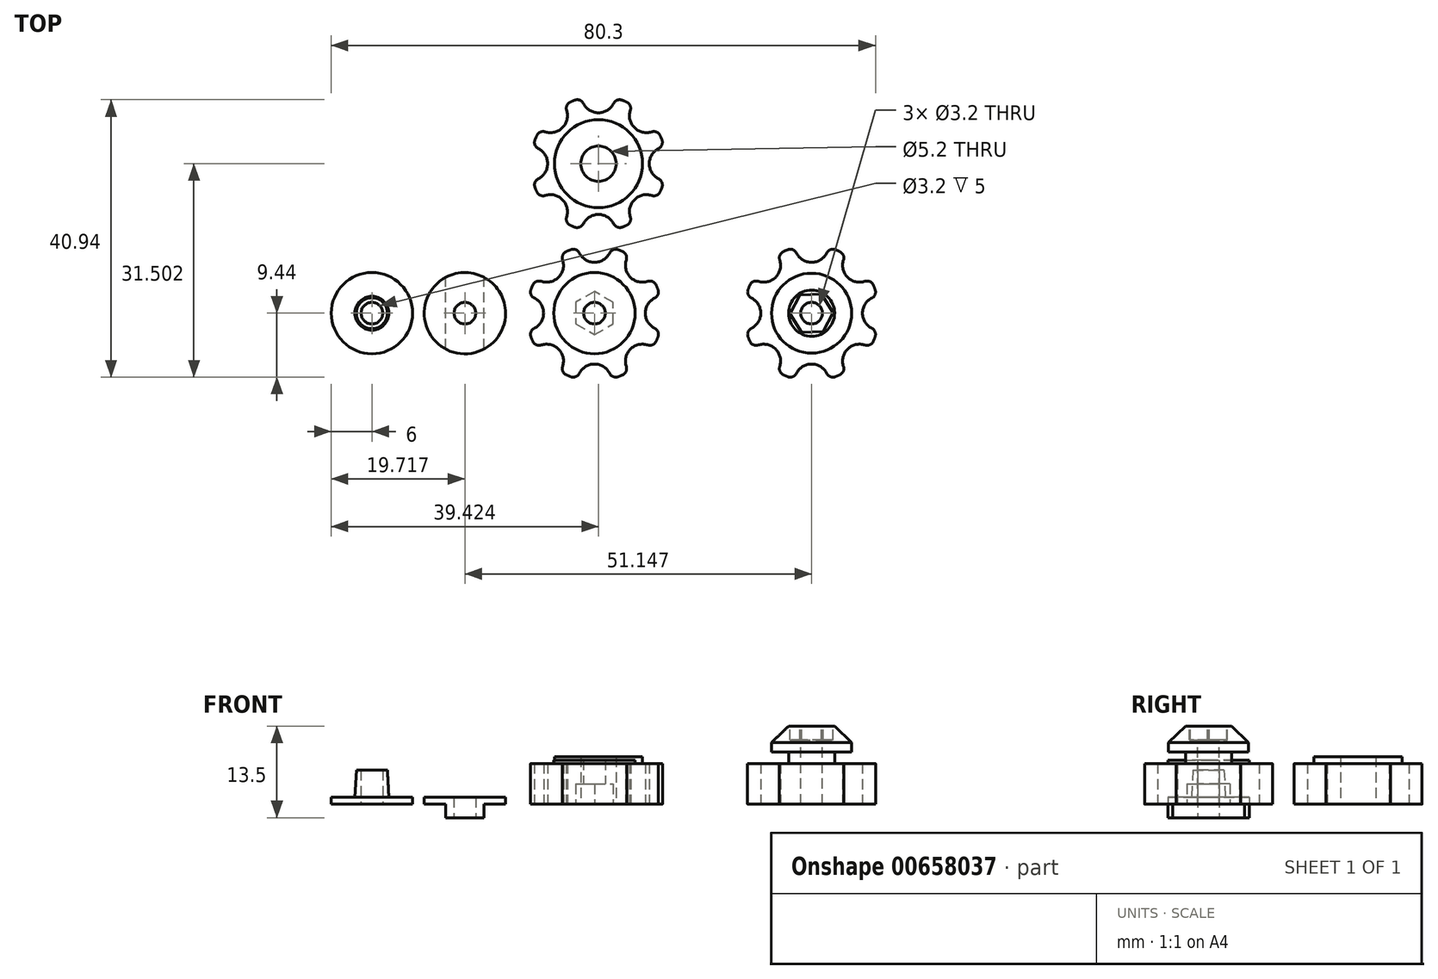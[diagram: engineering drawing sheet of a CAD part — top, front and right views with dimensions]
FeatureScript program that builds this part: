
annotation { "Feature Type Name" : "Feature", "Feature Type Description" : "" }
export const myFeature = defineFeature(function(context is Context, id is Id, definition is map)
    precondition{}
    {
        {
            var Q0;
            Q0=qCreatedBy(makeId("Top.planeOp"),FACE);
            var sketch = newSketch(context, id + "F0", { "sketchPlane" : qUnion([Q0])});
            skCircle(sketch, "E0", {"center": v(0, 0) * mm, "radius": 6 * mm});
            skSolve(sketch);
        }
        {
            var Q0;
            Q0 = qSketchRegion(id + "F0", true);
            extrude(context, id + "F1", {"entities" : qUnion([Q0]), "depth" : 1 * mm, "offsetDistance" : 25 * mm});
        }
        {
            var Q0;
            Q0=makeQuery(id+"F1.opExtrude","CAP_FACE",FACE,{"disambiguationData":[OSD([sQuery(id+"F0.wireOp",EDGE,"E0")])],"isStart":false});
            var sketch = newSketch(context, id + "F2", { "sketchPlane" : qUnion([Q0])});
            skCircle(sketch, "E1", {"center": v(0, 0) * mm, "radius": 2.5 * mm});
            skSolve(sketch);
        }
        {
            var Q0;
            Q0 = qSketchRegion(id + "F2", true);
            extrude(context, id + "F3", {"entities" : qUnion([Q0]), "operationType" : NewBodyOperationType.ADD, "depth" : 4 * mm, "offsetDistance" : 25 * mm, "hasDraft" : true, "draftAngle" : 3 * degree, "draftPullDirection" : true});
        }
        {
            var Q0;
            Q0=makeQuery(id+"F1.opExtrude","CAP_FACE",FACE,{"disambiguationData":[OSD([sQuery(id+"F0.wireOp",EDGE,"E0")])],"isStart":true});
            var sketch = newSketch(context, id + "F4", { "sketchPlane" : qUnion([Q0])});
            skCircle(sketch, "E2", {"center": v(0, 0) * mm, "radius": 1.6 * mm});
            skSolve(sketch);
        }
        {
            var Q0;
            Q0 = qSketchRegion(id + "F4", true);
            extrude(context, id + "F5", {"entities" : qUnion([Q0]), "operationType" : NewBodyOperationType.REMOVE, "oppositeDirection" : true, "depth" : 25 * mm, "offsetDistance" : 25 * mm});
        }
        {
            var Q0;
            Q0=qCreatedBy(makeId("Top.planeOp"),FACE);
            var sketch = newSketch(context, id + "F6", { "sketchPlane" : qUnion([Q0])});
            skCircle(sketch, "E3", {"center": v(13.72, 0) * mm, "radius": 6 * mm});
            skCircle(sketch, "E4", {"center": v(13.72, 0) * mm, "radius": 1.6 * mm});
            skSolve(sketch);
        }
        {
            var Q0;
            Q0 = qSketchRegion(id + "F6", true);
            extrude(context, id + "F7", {"entities" : qUnion([Q0]), "depth" : 1 * mm, "offsetDistance" : 25 * mm});
        }
        {
            var Q0;
            Q0=makeQuery(id+"F7.opExtrude","CAP_FACE",FACE,{"disambiguationData":[OSD([sQuery(id+"F6.wireOp",EDGE,"E3"),sQuery(id+"F6.wireOp",EDGE,"E4")])],"isStart":true});
            var sketch = newSketch(context, id + "F8", { "sketchPlane" : qUnion([Q0])});
            skLineSegment(sketch, "E5", {"start": v(13.72, 0) * mm, "end": v(13.72, 6) * mm, "construction": true});
            skLineSegment(sketch, "E6", {"start": v(10.92, 5.3) * mm, "end": v(10.92, -5.3) * mm});
            skLineSegment(sketch, "E7.MirrorCS", {"start": v(16.52, 5.3) * mm, "end": v(16.52, -5.3) * mm});
            skArc(sketch, "E8", {"start": v(16.52, 5.3) * mm, "mid": v(13.72, 6) * mm, "end": v(10.92, 5.3) * mm, "construction": true});
            skArc(sketch, "E9.trimOffspring", {"start": v(10.92, -5.3) * mm, "mid": v(13.72, -6) * mm, "end": v(16.52, -5.3) * mm, "construction": true});
            skCircle(sketch, "E10", {"center": v(13.72, 0) * mm, "radius": 1.6 * mm});
            skSolve(sketch);
        }
        {
            var Q0;
            {var subQ0=sQuery(id+"F8.wireOp",EDGE,"E6");Q0=makeQuery(id+"F8.imprint","IMPRINT",FACE,{"disambiguationData":[TD([[makeQuery(id+"F8.imprint","IMPRINT",EDGE,{"derivedFrom":subQ0}),1.0]])]});}
            extrude(context, id + "F9", {"entities" : qUnion([Q0]), "operationType" : NewBodyOperationType.ADD, "depth" : 2 * mm, "offsetDistance" : 25 * mm});
        }
        {
            var Q0;
            Q0=qCreatedBy(makeId("Top.planeOp"),FACE);
            var sketch = newSketch(context, id + "F10", { "sketchPlane" : qUnion([Q0])});
            skArc(sketch, "E11", {"start": v(37, 9.09) * mm, "mid": v(36.66, 9.24) * mm, "end": v(36.31, 9.38) * mm});
            skCircle(sketch, "E12", {"center": v(32.83, 0) * mm, "radius": 1.6 * mm});
            skArc(sketch, "E13", {"start": v(41.72, 2.24) * mm, "mid": v(40.33, 0) * mm, "end": v(41.72, -2.24) * mm});
            skArc(sketch, "E14.1.0", {"start": v(37.53, 7.86) * mm, "mid": v(38.14, 5.3) * mm, "end": v(40.7, 4.7) * mm});
            skArc(sketch, "E14.2.0", {"start": v(30.6, 8.88) * mm, "mid": v(32.83, 7.5) * mm, "end": v(35.07, 8.88) * mm});
            skArc(sketch, "E14.3.0", {"start": v(24.97, 4.7) * mm, "mid": v(27.53, 5.3) * mm, "end": v(28.13, 7.86) * mm});
            skArc(sketch, "E14.4.0", {"start": v(23.95, -2.24) * mm, "mid": v(25.33, 0) * mm, "end": v(23.95, 2.24) * mm});
            skArc(sketch, "E14.5.0", {"start": v(28.13, -7.86) * mm, "mid": v(27.53, -5.3) * mm, "end": v(24.97, -4.7) * mm});
            skArc(sketch, "E14.6.0", {"start": v(35.07, -8.88) * mm, "mid": v(32.83, -7.5) * mm, "end": v(30.6, -8.88) * mm});
            skArc(sketch, "E14.7.0", {"start": v(40.7, -4.7) * mm, "mid": v(38.14, -5.3) * mm, "end": v(37.53, -7.86) * mm});
            skArc(sketch, "E15.trimOffspring", {"start": v(42.2, 3.48) * mm, "mid": v(42.07, 3.83) * mm, "end": v(41.92, 4.17) * mm});
            skArc(sketch, "E16.trimOffspring", {"start": v(41.92, -4.17) * mm, "mid": v(42.07, -3.83) * mm, "end": v(42.2, -3.48) * mm});
            skArc(sketch, "E17.trimOffspring", {"start": v(36.31, -9.38) * mm, "mid": v(36.66, -9.24) * mm, "end": v(37, -9.09) * mm});
            skArc(sketch, "E18.trimOffspring", {"start": v(28.66, -9.09) * mm, "mid": v(29, -9.24) * mm, "end": v(29.35, -9.38) * mm});
            skArc(sketch, "E19.trimOffspring", {"start": v(23.46, -3.48) * mm, "mid": v(23.6, -3.83) * mm, "end": v(23.74, -4.17) * mm});
            skArc(sketch, "E20.trimOffspring", {"start": v(23.74, 4.17) * mm, "mid": v(23.6, 3.83) * mm, "end": v(23.46, 3.48) * mm});
            skArc(sketch, "E21.trimOffspring", {"start": v(29.35, 9.38) * mm, "mid": v(29, 9.24) * mm, "end": v(28.66, 9.09) * mm});
            skPoint(sketch, "E22.visualSharp", {"position": v(37.93, 8.6) * mm});
            skArc(sketch, "E22.filletArc", {"start": v(37.53, 7.86) * mm, "mid": v(37.5, 8.58) * mm, "end": v(37, 9.09) * mm});
            skPoint(sketch, "E23.visualSharp", {"position": v(35.31, 9.69) * mm});
            skArc(sketch, "E23.filletArc", {"start": v(36.31, 9.38) * mm, "mid": v(35.6, 9.37) * mm, "end": v(35.07, 8.88) * mm});
            skPoint(sketch, "E24.visualSharp", {"position": v(30.35, 9.69) * mm});
            skArc(sketch, "E24.filletArc", {"start": v(30.6, 8.88) * mm, "mid": v(30.07, 9.37) * mm, "end": v(29.35, 9.38) * mm});
            skPoint(sketch, "E25.visualSharp", {"position": v(27.74, 8.6) * mm});
            skArc(sketch, "E25.filletArc", {"start": v(28.66, 9.09) * mm, "mid": v(28.16, 8.58) * mm, "end": v(28.13, 7.86) * mm});
            skPoint(sketch, "E26.visualSharp", {"position": v(24.23, 5.1) * mm});
            skArc(sketch, "E26.filletArc", {"start": v(24.97, 4.7) * mm, "mid": v(24.25, 4.67) * mm, "end": v(23.74, 4.17) * mm});
            skPoint(sketch, "E27.visualSharp", {"position": v(23.15, 2.48) * mm});
            skArc(sketch, "E27.filletArc", {"start": v(23.46, 3.48) * mm, "mid": v(23.47, 2.76) * mm, "end": v(23.95, 2.24) * mm});
            skPoint(sketch, "E28.visualSharp", {"position": v(23.15, -2.48) * mm});
            skArc(sketch, "E28.filletArc", {"start": v(23.95, -2.24) * mm, "mid": v(23.47, -2.76) * mm, "end": v(23.46, -3.48) * mm});
            skPoint(sketch, "E29.visualSharp", {"position": v(24.23, -5.1) * mm});
            skArc(sketch, "E29.filletArc", {"start": v(23.74, -4.17) * mm, "mid": v(24.25, -4.67) * mm, "end": v(24.97, -4.7) * mm});
            skPoint(sketch, "E30.visualSharp", {"position": v(27.74, -8.6) * mm});
            skArc(sketch, "E30.filletArc", {"start": v(28.13, -7.86) * mm, "mid": v(28.16, -8.58) * mm, "end": v(28.66, -9.09) * mm});
            skPoint(sketch, "E31.visualSharp", {"position": v(30.35, -9.69) * mm});
            skArc(sketch, "E31.filletArc", {"start": v(29.35, -9.38) * mm, "mid": v(30.07, -9.37) * mm, "end": v(30.6, -8.88) * mm});
            skPoint(sketch, "E32.visualSharp", {"position": v(35.31, -9.69) * mm});
            skArc(sketch, "E32.filletArc", {"start": v(35.07, -8.88) * mm, "mid": v(35.6, -9.37) * mm, "end": v(36.31, -9.38) * mm});
            skPoint(sketch, "E33.visualSharp", {"position": v(37.93, -8.6) * mm});
            skArc(sketch, "E33.filletArc", {"start": v(37, -9.09) * mm, "mid": v(37.5, -8.58) * mm, "end": v(37.53, -7.86) * mm});
            skPoint(sketch, "E34.visualSharp", {"position": v(41.44, -5.1) * mm});
            skArc(sketch, "E34.filletArc", {"start": v(40.7, -4.7) * mm, "mid": v(41.41, -4.67) * mm, "end": v(41.92, -4.17) * mm});
            skPoint(sketch, "E35.visualSharp", {"position": v(42.52, -2.48) * mm});
            skArc(sketch, "E35.filletArc", {"start": v(42.2, -3.48) * mm, "mid": v(42.2, -2.76) * mm, "end": v(41.72, -2.24) * mm});
            skPoint(sketch, "E36.visualSharp", {"position": v(42.52, 2.48) * mm});
            skArc(sketch, "E36.filletArc", {"start": v(41.72, 2.24) * mm, "mid": v(42.2, 2.76) * mm, "end": v(42.2, 3.48) * mm});
            skPoint(sketch, "E37.visualSharp", {"position": v(41.44, 5.1) * mm});
            skArc(sketch, "E37.filletArc", {"start": v(41.92, 4.17) * mm, "mid": v(41.41, 4.67) * mm, "end": v(40.7, 4.7) * mm});
            skSolve(sketch);
        }
        {
            var Q0;
            Q0 = qSketchRegion(id + "F10", true);
            extrude(context, id + "F11", {"entities" : qUnion([Q0]), "depth" : 6 * mm, "offsetDistance" : 25 * mm});
        }
        {
            var Q0;
            Q0=makeQuery(id+"F11.opExtrude","CAP_FACE",FACE,{"disambiguationData":[OSD([sQuery(id+"F10.wireOp",EDGE,"E11"),sQuery(id+"F10.wireOp",EDGE,"E12"),sQuery(id+"F10.wireOp",EDGE,"E13"),sQuery(id+"F10.wireOp",EDGE,"E14.1.0"),sQuery(id+"F10.wireOp",EDGE,"E14.2.0"),sQuery(id+"F10.wireOp",EDGE,"E14.3.0"),sQuery(id+"F10.wireOp",EDGE,"E14.4.0"),sQuery(id+"F10.wireOp",EDGE,"E14.5.0"),sQuery(id+"F10.wireOp",EDGE,"E14.6.0"),sQuery(id+"F10.wireOp",EDGE,"E14.7.0"),sQuery(id+"F10.wireOp",EDGE,"E15.trimOffspring"),sQuery(id+"F10.wireOp",EDGE,"E16.trimOffspring"),sQuery(id+"F10.wireOp",EDGE,"E17.trimOffspring"),sQuery(id+"F10.wireOp",EDGE,"E18.trimOffspring"),sQuery(id+"F10.wireOp",EDGE,"E19.trimOffspring"),sQuery(id+"F10.wireOp",EDGE,"E20.trimOffspring"),sQuery(id+"F10.wireOp",EDGE,"E21.trimOffspring"),sQuery(id+"F10.wireOp",EDGE,"E22.filletArc"),sQuery(id+"F10.wireOp",EDGE,"E23.filletArc"),sQuery(id+"F10.wireOp",EDGE,"E24.filletArc"),sQuery(id+"F10.wireOp",EDGE,"E25.filletArc"),sQuery(id+"F10.wireOp",EDGE,"E26.filletArc"),sQuery(id+"F10.wireOp",EDGE,"E27.filletArc"),sQuery(id+"F10.wireOp",EDGE,"E28.filletArc"),sQuery(id+"F10.wireOp",EDGE,"E29.filletArc"),sQuery(id+"F10.wireOp",EDGE,"E30.filletArc"),sQuery(id+"F10.wireOp",EDGE,"E31.filletArc"),sQuery(id+"F10.wireOp",EDGE,"E32.filletArc"),sQuery(id+"F10.wireOp",EDGE,"E33.filletArc"),sQuery(id+"F10.wireOp",EDGE,"E34.filletArc"),sQuery(id+"F10.wireOp",EDGE,"E35.filletArc"),sQuery(id+"F10.wireOp",EDGE,"E36.filletArc"),sQuery(id+"F10.wireOp",EDGE,"E37.filletArc")])],"isStart":false});
            var sketch = newSketch(context, id + "F12", { "sketchPlane" : qUnion([Q0])});
            skCircle(sketch, "E38", {"center": v(32.83, 0) * mm, "radius": 1.6 * mm});
            skCircle(sketch, "E39", {"center": v(32.83, 0) * mm, "radius": 6 * mm});
            skSolve(sketch);
        }
        {
            var Q0;
            Q0=makeQuery(id+"F12.imprint","IMPRINT",FACE,{"disambiguationData":[TD([[makeQuery(id+"F12.imprint","IMPRINT",EDGE,{"derivedFrom":sQuery(id+"F12.wireOp",EDGE,"E38")}),-1.0]])]});
            extrude(context, id + "F13", {"entities" : qUnion([Q0]), "operationType" : NewBodyOperationType.ADD, "depth" : 0.5 * mm, "offsetDistance" : 25 * mm});
        }
        {
            var Q0;
            Q0=makeQuery(id+"F11.opExtrude","CAP_FACE",FACE,{"disambiguationData":[OSD([sQuery(id+"F10.wireOp",EDGE,"E11"),sQuery(id+"F10.wireOp",EDGE,"E12"),sQuery(id+"F10.wireOp",EDGE,"E13"),sQuery(id+"F10.wireOp",EDGE,"E14.1.0"),sQuery(id+"F10.wireOp",EDGE,"E14.2.0"),sQuery(id+"F10.wireOp",EDGE,"E14.3.0"),sQuery(id+"F10.wireOp",EDGE,"E14.4.0"),sQuery(id+"F10.wireOp",EDGE,"E14.5.0"),sQuery(id+"F10.wireOp",EDGE,"E14.6.0"),sQuery(id+"F10.wireOp",EDGE,"E14.7.0"),sQuery(id+"F10.wireOp",EDGE,"E15.trimOffspring"),sQuery(id+"F10.wireOp",EDGE,"E16.trimOffspring"),sQuery(id+"F10.wireOp",EDGE,"E17.trimOffspring"),sQuery(id+"F10.wireOp",EDGE,"E18.trimOffspring"),sQuery(id+"F10.wireOp",EDGE,"E19.trimOffspring"),sQuery(id+"F10.wireOp",EDGE,"E20.trimOffspring"),sQuery(id+"F10.wireOp",EDGE,"E21.trimOffspring"),sQuery(id+"F10.wireOp",EDGE,"E22.filletArc"),sQuery(id+"F10.wireOp",EDGE,"E23.filletArc"),sQuery(id+"F10.wireOp",EDGE,"E24.filletArc"),sQuery(id+"F10.wireOp",EDGE,"E25.filletArc"),sQuery(id+"F10.wireOp",EDGE,"E26.filletArc"),sQuery(id+"F10.wireOp",EDGE,"E27.filletArc"),sQuery(id+"F10.wireOp",EDGE,"E28.filletArc"),sQuery(id+"F10.wireOp",EDGE,"E29.filletArc"),sQuery(id+"F10.wireOp",EDGE,"E30.filletArc"),sQuery(id+"F10.wireOp",EDGE,"E31.filletArc"),sQuery(id+"F10.wireOp",EDGE,"E32.filletArc"),sQuery(id+"F10.wireOp",EDGE,"E33.filletArc"),sQuery(id+"F10.wireOp",EDGE,"E34.filletArc"),sQuery(id+"F10.wireOp",EDGE,"E35.filletArc"),sQuery(id+"F10.wireOp",EDGE,"E36.filletArc"),sQuery(id+"F10.wireOp",EDGE,"E37.filletArc")])],"isStart":true});
            var sketch = newSketch(context, id + "F14", { "sketchPlane" : qUnion([Q0])});
            skCircle(sketch, "E40.cCircle", {"center": v(32.83, 0) * mm, "radius": 2.75 * mm, "construction": true});
            skLineSegment(sketch, "E40.0", {"start": v(35.58, 1.59) * mm, "end": v(35.58, -1.59) * mm});
            skLineSegment(sketch, "E40.1", {"start": v(35.58, -1.59) * mm, "end": v(32.83, -3.18) * mm});
            skLineSegment(sketch, "E40.2", {"start": v(32.83, -3.18) * mm, "end": v(30.08, -1.59) * mm});
            skLineSegment(sketch, "E40.3", {"start": v(30.08, -1.59) * mm, "end": v(30.08, 1.59) * mm});
            skLineSegment(sketch, "E40.4", {"start": v(30.08, 1.59) * mm, "end": v(32.83, 3.18) * mm});
            skLineSegment(sketch, "E40.5", {"start": v(32.83, 3.18) * mm, "end": v(35.58, 1.59) * mm});
            skPoint(sketch, "E40.0.midPoint", {"position": v(35.58, 0) * mm});
            skSolve(sketch);
        }
        {
            var Q0;
            Q0 = qSketchRegion(id + "F14", true);
            extrude(context, id + "F15", {"entities" : qUnion([Q0]), "operationType" : NewBodyOperationType.REMOVE, "oppositeDirection" : true, "depth" : 3 * mm, "offsetDistance" : 25 * mm});
        }
        {
            var Q0;
            Q0=qCreatedBy(makeId("Front.planeOp"),FACE);
            var sketch = newSketch(context, id + "F16", { "sketchPlane" : qUnion([Q0])});
            skLineSegment(sketch, "E41", {"start": v(64.86, 11.5) * mm, "end": v(68.26, 11.5) * mm});
            skLineSegment(sketch, "E42", {"start": v(68.26, 11.5) * mm, "end": v(70.76, 9.1) * mm});
            skLineSegment(sketch, "E43", {"start": v(70.76, 9.1) * mm, "end": v(70.76, 7.7) * mm});
            skLineSegment(sketch, "E44", {"start": v(70.76, 7.7) * mm, "end": v(68.26, 7.7) * mm});
            skLineSegment(sketch, "E45", {"start": v(68.26, 7.7) * mm, "end": v(68.26, 6) * mm});
            skLineSegment(sketch, "E46", {"start": v(68.26, 6) * mm, "end": v(74.86, 6) * mm});
            skLineSegment(sketch, "E47", {"start": v(74.86, 6) * mm, "end": v(74.86, 0) * mm});
            skLineSegment(sketch, "E48", {"start": v(74.86, 0) * mm, "end": v(64.86, 0) * mm});
            skLineSegment(sketch, "E49", {"start": v(64.86, 0) * mm, "end": v(64.86, 11.5) * mm});
            skSolve(sketch);
        }
        {
            var Q0;
            Q0 = qSketchRegion(id + "F16", true);
            var Q1;
            Q1=sQuery(id+"F16.wireOp",EDGE,"E49");
            revolve(context, id + "F17", {"operationType" : NewBodyOperationType.ADD, "surfaceOperationType" : NewSurfaceOperationType.NEW, "entities" : qUnion([Q0]), "axis" : qUnion([Q1]), "revolveType" : RevolveType.FULL});
        }
        {
            var Q0;
            Q0=makeQuery(id+"F17.opRevolve","SWEPT_FACE",FACE,{"disambiguationData":[OSD([sQuery(id+"F16.wireOp",EDGE,"E41")])]});
            var sketch = newSketch(context, id + "F18", { "sketchPlane" : qUnion([Q0])});
            skCircle(sketch, "E50", {"center": v(64.86, 0) * mm, "radius": 1.6 * mm});
            skSolve(sketch);
        }
        {
            var Q0;
            Q0 = qSketchRegion(id + "F18", true);
            extrude(context, id + "F19", {"entities" : qUnion([Q0]), "operationType" : NewBodyOperationType.REMOVE, "oppositeDirection" : true, "depth" : 25 * mm, "offsetDistance" : 25 * mm});
        }
        {
            var Q0;
            Q0=makeQuery(id+"F17.opRevolve","SWEPT_FACE",FACE,{"disambiguationData":[OSD([sQuery(id+"F16.wireOp",EDGE,"E41")])]});
            var sketch = newSketch(context, id + "F20", { "sketchPlane" : qUnion([Q0])});
            skCircle(sketch, "E51.cCircle", {"center": v(64.86, 0) * mm, "radius": 2.75 * mm, "construction": true});
            skLineSegment(sketch, "E51.0", {"start": v(68.04, 0.12) * mm, "end": v(66.56, -2.69) * mm});
            skLineSegment(sketch, "E51.1", {"start": v(66.56, -2.69) * mm, "end": v(63.38, -2.8) * mm});
            skLineSegment(sketch, "E51.2", {"start": v(63.38, -2.8) * mm, "end": v(61.7, -0.12) * mm});
            skLineSegment(sketch, "E51.3", {"start": v(61.7, -0.12) * mm, "end": v(63.17, 2.69) * mm});
            skLineSegment(sketch, "E51.4", {"start": v(63.17, 2.69) * mm, "end": v(66.34, 2.8) * mm});
            skLineSegment(sketch, "E51.5", {"start": v(66.34, 2.8) * mm, "end": v(68.04, 0.12) * mm});
            skPoint(sketch, "E51.0.midPoint", {"position": v(67.3, -1.28) * mm});
            skSolve(sketch);
        }
        {
            var Q0;
            Q0 = qSketchRegion(id + "F20", true);
            extrude(context, id + "F21", {"entities" : qUnion([Q0]), "operationType" : NewBodyOperationType.REMOVE, "oppositeDirection" : true, "depth" : 2 * mm, "offsetDistance" : 25 * mm});
        }
        {
            var Q0;
            Q0=makeQuery(id+"F17.opRevolve","SWEPT_FACE",FACE,{"disambiguationData":[OSD([sQuery(id+"F16.wireOp",EDGE,"E48")])]});
            var sketch = newSketch(context, id + "F22", { "sketchPlane" : qUnion([Q0])});
            skLineSegment(sketch, "E52", {"start": v(64.86, 0) * mm, "end": v(64.86, 15.9) * mm, "construction": true});
            skArc(sketch, "E53", {"start": v(62.63, 8.88) * mm, "mid": v(64.86, 7.5) * mm, "end": v(67.1, 8.88) * mm});
            skArc(sketch, "E54.1.0", {"start": v(57, 4.7) * mm, "mid": v(59.56, 5.3) * mm, "end": v(60.16, 7.86) * mm});
            skArc(sketch, "E54.2.0", {"start": v(55.98, -2.24) * mm, "mid": v(57.36, 0) * mm, "end": v(55.98, 2.24) * mm});
            skArc(sketch, "E54.3.0", {"start": v(60.16, -7.86) * mm, "mid": v(59.56, -5.3) * mm, "end": v(57, -4.7) * mm});
            skArc(sketch, "E54.4.0", {"start": v(67.1, -8.88) * mm, "mid": v(64.86, -7.5) * mm, "end": v(62.63, -8.88) * mm});
            skArc(sketch, "E54.5.0", {"start": v(72.73, -4.7) * mm, "mid": v(70.17, -5.3) * mm, "end": v(69.56, -7.86) * mm});
            skArc(sketch, "E54.6.0", {"start": v(73.75, 2.24) * mm, "mid": v(72.36, 0) * mm, "end": v(73.75, -2.24) * mm});
            skArc(sketch, "E54.7.0", {"start": v(69.56, 7.86) * mm, "mid": v(70.17, 5.3) * mm, "end": v(72.73, 4.7) * mm});
            skPoint(sketch, "E54.center", {"position": v(64.86, 0) * mm});
            skArc(sketch, "E55", {"start": v(61.38, 9.38) * mm, "mid": v(61.04, 9.24) * mm, "end": v(60.7, 9.09) * mm});
            skArc(sketch, "E56.trimOffspring", {"start": v(69.03, 9.09) * mm, "mid": v(68.7, 9.24) * mm, "end": v(68.34, 9.37) * mm});
            skArc(sketch, "E57.trimOffspring", {"start": v(74.24, 3.48) * mm, "mid": v(74.1, 3.83) * mm, "end": v(73.95, 4.17) * mm});
            skArc(sketch, "E58.trimOffspring", {"start": v(73.95, -4.17) * mm, "mid": v(74.1, -3.83) * mm, "end": v(74.24, -3.48) * mm});
            skArc(sketch, "E59.trimOffspring", {"start": v(68.34, -9.37) * mm, "mid": v(68.7, -9.24) * mm, "end": v(69.03, -9.09) * mm});
            skArc(sketch, "E60.trimOffspring", {"start": v(55.77, 4.17) * mm, "mid": v(55.62, 3.83) * mm, "end": v(55.49, 3.48) * mm});
            skArc(sketch, "E61.trimOffspring", {"start": v(55.49, -3.48) * mm, "mid": v(55.62, -3.83) * mm, "end": v(55.77, -4.17) * mm});
            skPoint(sketch, "E62.visualSharp", {"position": v(67.34, 9.69) * mm});
            skArc(sketch, "E62.filletArc", {"start": v(68.34, 9.37) * mm, "mid": v(67.63, 9.37) * mm, "end": v(67.1, 8.88) * mm});
            skPoint(sketch, "E63.visualSharp", {"position": v(69.96, 8.6) * mm});
            skArc(sketch, "E63.filletArc", {"start": v(69.56, 7.86) * mm, "mid": v(69.53, 8.58) * mm, "end": v(69.03, 9.09) * mm});
            skPoint(sketch, "E64.visualSharp", {"position": v(73.47, 5.1) * mm});
            skArc(sketch, "E64.filletArc", {"start": v(73.95, 4.17) * mm, "mid": v(73.44, 4.67) * mm, "end": v(72.73, 4.7) * mm});
            skPoint(sketch, "E65.visualSharp", {"position": v(74.55, 2.48) * mm});
            skArc(sketch, "E65.filletArc", {"start": v(73.75, 2.24) * mm, "mid": v(74.23, 2.76) * mm, "end": v(74.24, 3.48) * mm});
            skPoint(sketch, "E66.visualSharp", {"position": v(74.55, -2.48) * mm});
            skArc(sketch, "E66.filletArc", {"start": v(74.24, -3.48) * mm, "mid": v(74.23, -2.76) * mm, "end": v(73.75, -2.24) * mm});
            skPoint(sketch, "E67.visualSharp", {"position": v(73.47, -5.1) * mm});
            skArc(sketch, "E67.filletArc", {"start": v(72.73, -4.7) * mm, "mid": v(73.44, -4.67) * mm, "end": v(73.95, -4.17) * mm});
            skPoint(sketch, "E68.visualSharp", {"position": v(69.96, -8.6) * mm});
            skArc(sketch, "E68.filletArc", {"start": v(69.03, -9.09) * mm, "mid": v(69.53, -8.58) * mm, "end": v(69.56, -7.86) * mm});
            skPoint(sketch, "E69.visualSharp", {"position": v(67.34, -9.69) * mm});
            skArc(sketch, "E69.filletArc", {"start": v(67.1, -8.88) * mm, "mid": v(67.63, -9.37) * mm, "end": v(68.34, -9.37) * mm});
            skArc(sketch, "E70", {"start": v(60.7, -9.09) * mm, "mid": v(61.04, -9.24) * mm, "end": v(61.38, -9.38) * mm});
            skPoint(sketch, "E71.visualSharp", {"position": v(62.38, -9.69) * mm});
            skArc(sketch, "E71.filletArc", {"start": v(61.38, -9.37) * mm, "mid": v(62.1, -9.37) * mm, "end": v(62.63, -8.88) * mm});
            skPoint(sketch, "E72.visualSharp", {"position": v(59.77, -8.6) * mm});
            skArc(sketch, "E72.filletArc", {"start": v(60.16, -7.86) * mm, "mid": v(60.2, -8.58) * mm, "end": v(60.7, -9.09) * mm});
            skPoint(sketch, "E73.visualSharp", {"position": v(56.26, -5.1) * mm});
            skArc(sketch, "E73.filletArc", {"start": v(55.77, -4.17) * mm, "mid": v(56.29, -4.67) * mm, "end": v(57, -4.7) * mm});
            skPoint(sketch, "E74.visualSharp", {"position": v(55.18, -2.48) * mm});
            skArc(sketch, "E74.filletArc", {"start": v(55.98, -2.24) * mm, "mid": v(55.5, -2.76) * mm, "end": v(55.49, -3.48) * mm});
            skPoint(sketch, "E75.visualSharp", {"position": v(55.18, 2.48) * mm});
            skArc(sketch, "E75.filletArc", {"start": v(55.49, 3.48) * mm, "mid": v(55.5, 2.76) * mm, "end": v(55.98, 2.24) * mm});
            skPoint(sketch, "E76.visualSharp", {"position": v(56.26, 5.1) * mm});
            skArc(sketch, "E76.filletArc", {"start": v(57, 4.7) * mm, "mid": v(56.29, 4.67) * mm, "end": v(55.77, 4.17) * mm});
            skPoint(sketch, "E77.visualSharp", {"position": v(59.77, 8.6) * mm});
            skArc(sketch, "E77.filletArc", {"start": v(60.7, 9.09) * mm, "mid": v(60.2, 8.58) * mm, "end": v(60.16, 7.86) * mm});
            skPoint(sketch, "E78.visualSharp", {"position": v(62.38, 9.69) * mm});
            skArc(sketch, "E78.filletArc", {"start": v(62.63, 8.88) * mm, "mid": v(62.1, 9.37) * mm, "end": v(61.38, 9.38) * mm});
            skCircle(sketch, "E79", {"center": v(64.86, 0) * mm, "radius": 13.38 * mm});
            skSolve(sketch);
        }
        {
            var Q0;
            Q0 = qSketchRegion(id + "F22", true);
            extrude(context, id + "F23", {"entities" : qUnion([Q0]), "operationType" : NewBodyOperationType.REMOVE, "oppositeDirection" : true, "depth" : 25 * mm, "offsetDistance" : 25 * mm});
        }
        {
            var Q0;
            Q0=qCreatedBy(makeId("Top.planeOp"),FACE);
            var sketch = newSketch(context, id + "F24", { "sketchPlane" : qUnion([Q0])});
            skArc(sketch, "E80", {"start": v(37.6, 31.15) * mm, "mid": v(37.25, 31.3) * mm, "end": v(36.9, 31.44) * mm});
            skCircle(sketch, "E81", {"center": v(33.42, 22.06) * mm, "radius": 2.6 * mm});
            skArc(sketch, "E82", {"start": v(42.3, 24.3) * mm, "mid": v(40.92, 22.06) * mm, "end": v(42.3, 19.83) * mm});
            skArc(sketch, "E83.1.0", {"start": v(38.12, 29.93) * mm, "mid": v(38.73, 27.37) * mm, "end": v(41.29, 26.76) * mm});
            skArc(sketch, "E83.2.0", {"start": v(31.19, 30.95) * mm, "mid": v(33.42, 29.56) * mm, "end": v(35.66, 30.95) * mm});
            skArc(sketch, "E83.3.0", {"start": v(25.56, 26.76) * mm, "mid": v(28.12, 27.37) * mm, "end": v(28.72, 29.93) * mm});
            skArc(sketch, "E83.4.0", {"start": v(24.54, 19.83) * mm, "mid": v(25.92, 22.06) * mm, "end": v(24.54, 24.3) * mm});
            skArc(sketch, "E83.5.0", {"start": v(28.72, 14.2) * mm, "mid": v(28.12, 16.76) * mm, "end": v(25.56, 17.36) * mm});
            skArc(sketch, "E83.6.0", {"start": v(35.66, 13.18) * mm, "mid": v(33.42, 14.56) * mm, "end": v(31.19, 13.18) * mm});
            skArc(sketch, "E83.7.0", {"start": v(41.29, 17.36) * mm, "mid": v(38.73, 16.76) * mm, "end": v(38.12, 14.2) * mm});
            skArc(sketch, "E84.trimOffspring", {"start": v(42.8, 25.54) * mm, "mid": v(42.66, 25.89) * mm, "end": v(42.51, 26.23) * mm});
            skArc(sketch, "E85.trimOffspring", {"start": v(42.51, 17.9) * mm, "mid": v(42.66, 18.24) * mm, "end": v(42.8, 18.58) * mm});
            skArc(sketch, "E86.trimOffspring", {"start": v(36.9, 12.69) * mm, "mid": v(37.25, 12.82) * mm, "end": v(37.6, 12.97) * mm});
            skArc(sketch, "E87.trimOffspring", {"start": v(29.26, 12.97) * mm, "mid": v(29.6, 12.82) * mm, "end": v(29.94, 12.69) * mm});
            skArc(sketch, "E88.trimOffspring", {"start": v(24.05, 18.58) * mm, "mid": v(24.19, 18.24) * mm, "end": v(24.33, 17.9) * mm});
            skArc(sketch, "E89.trimOffspring", {"start": v(24.33, 26.23) * mm, "mid": v(24.19, 25.89) * mm, "end": v(24.05, 25.54) * mm});
            skArc(sketch, "E90.trimOffspring", {"start": v(29.94, 31.44) * mm, "mid": v(29.6, 31.3) * mm, "end": v(29.26, 31.15) * mm});
            skPoint(sketch, "E91.visualSharp", {"position": v(38.52, 30.67) * mm});
            skArc(sketch, "E91.filletArc", {"start": v(38.12, 29.93) * mm, "mid": v(38.1, 30.64) * mm, "end": v(37.6, 31.15) * mm});
            skPoint(sketch, "E92.visualSharp", {"position": v(35.9, 31.75) * mm});
            skArc(sketch, "E92.filletArc", {"start": v(36.9, 31.44) * mm, "mid": v(36.19, 31.43) * mm, "end": v(35.66, 30.95) * mm});
            skPoint(sketch, "E93.visualSharp", {"position": v(30.94, 31.75) * mm});
            skArc(sketch, "E93.filletArc", {"start": v(31.19, 30.95) * mm, "mid": v(30.66, 31.43) * mm, "end": v(29.94, 31.44) * mm});
            skPoint(sketch, "E94.visualSharp", {"position": v(28.33, 30.67) * mm});
            skArc(sketch, "E94.filletArc", {"start": v(29.26, 31.15) * mm, "mid": v(28.75, 30.64) * mm, "end": v(28.72, 29.93) * mm});
            skPoint(sketch, "E95.visualSharp", {"position": v(24.82, 27.16) * mm});
            skArc(sketch, "E95.filletArc", {"start": v(25.56, 26.76) * mm, "mid": v(24.85, 26.73) * mm, "end": v(24.33, 26.23) * mm});
            skPoint(sketch, "E96.visualSharp", {"position": v(23.74, 24.54) * mm});
            skArc(sketch, "E96.filletArc", {"start": v(24.05, 25.54) * mm, "mid": v(24.06, 24.83) * mm, "end": v(24.54, 24.3) * mm});
            skPoint(sketch, "E97.visualSharp", {"position": v(23.74, 19.58) * mm});
            skArc(sketch, "E97.filletArc", {"start": v(24.54, 19.83) * mm, "mid": v(24.06, 19.3) * mm, "end": v(24.05, 18.58) * mm});
            skPoint(sketch, "E98.visualSharp", {"position": v(24.82, 16.97) * mm});
            skArc(sketch, "E98.filletArc", {"start": v(24.33, 17.9) * mm, "mid": v(24.85, 17.4) * mm, "end": v(25.56, 17.36) * mm});
            skPoint(sketch, "E99.visualSharp", {"position": v(28.33, 13.46) * mm});
            skArc(sketch, "E99.filletArc", {"start": v(28.72, 14.2) * mm, "mid": v(28.75, 13.48) * mm, "end": v(29.26, 12.97) * mm});
            skPoint(sketch, "E100.visualSharp", {"position": v(30.94, 12.37) * mm});
            skArc(sketch, "E100.filletArc", {"start": v(29.94, 12.69) * mm, "mid": v(30.66, 12.7) * mm, "end": v(31.19, 13.18) * mm});
            skPoint(sketch, "E101.visualSharp", {"position": v(35.9, 12.37) * mm});
            skArc(sketch, "E101.filletArc", {"start": v(35.66, 13.18) * mm, "mid": v(36.19, 12.7) * mm, "end": v(36.9, 12.69) * mm});
            skPoint(sketch, "E102.visualSharp", {"position": v(38.52, 13.46) * mm});
            skArc(sketch, "E102.filletArc", {"start": v(37.6, 12.97) * mm, "mid": v(38.1, 13.48) * mm, "end": v(38.12, 14.2) * mm});
            skPoint(sketch, "E103.visualSharp", {"position": v(42.03, 16.97) * mm});
            skArc(sketch, "E103.filletArc", {"start": v(41.29, 17.36) * mm, "mid": v(42, 17.4) * mm, "end": v(42.51, 17.9) * mm});
            skPoint(sketch, "E104.visualSharp", {"position": v(43.11, 19.58) * mm});
            skArc(sketch, "E104.filletArc", {"start": v(42.8, 18.58) * mm, "mid": v(42.8, 19.3) * mm, "end": v(42.3, 19.83) * mm});
            skPoint(sketch, "E105.visualSharp", {"position": v(43.11, 24.54) * mm});
            skArc(sketch, "E105.filletArc", {"start": v(42.3, 24.3) * mm, "mid": v(42.8, 24.83) * mm, "end": v(42.8, 25.54) * mm});
            skPoint(sketch, "E106.visualSharp", {"position": v(42.03, 27.16) * mm});
            skArc(sketch, "E106.filletArc", {"start": v(42.51, 26.23) * mm, "mid": v(42, 26.73) * mm, "end": v(41.29, 26.76) * mm});
            skSolve(sketch);
        }
        {
            var Q0;
            Q0 = qSketchRegion(id + "F24", true);
            extrude(context, id + "F25", {"entities" : qUnion([Q0]), "depth" : 6 * mm, "offsetDistance" : 25 * mm});
        }
        {
            var Q0;
            Q0=makeQuery(id+"F25.opExtrude","CAP_FACE",FACE,{"disambiguationData":[OSD([sQuery(id+"F24.wireOp",EDGE,"E80"),sQuery(id+"F24.wireOp",EDGE,"E81"),sQuery(id+"F24.wireOp",EDGE,"E82"),sQuery(id+"F24.wireOp",EDGE,"E83.1.0"),sQuery(id+"F24.wireOp",EDGE,"E83.2.0"),sQuery(id+"F24.wireOp",EDGE,"E83.3.0"),sQuery(id+"F24.wireOp",EDGE,"E83.4.0"),sQuery(id+"F24.wireOp",EDGE,"E83.5.0"),sQuery(id+"F24.wireOp",EDGE,"E83.6.0"),sQuery(id+"F24.wireOp",EDGE,"E83.7.0"),sQuery(id+"F24.wireOp",EDGE,"E84.trimOffspring"),sQuery(id+"F24.wireOp",EDGE,"E85.trimOffspring"),sQuery(id+"F24.wireOp",EDGE,"E86.trimOffspring"),sQuery(id+"F24.wireOp",EDGE,"E87.trimOffspring"),sQuery(id+"F24.wireOp",EDGE,"E88.trimOffspring"),sQuery(id+"F24.wireOp",EDGE,"E89.trimOffspring"),sQuery(id+"F24.wireOp",EDGE,"E90.trimOffspring"),sQuery(id+"F24.wireOp",EDGE,"E91.filletArc"),sQuery(id+"F24.wireOp",EDGE,"E92.filletArc"),sQuery(id+"F24.wireOp",EDGE,"E93.filletArc"),sQuery(id+"F24.wireOp",EDGE,"E94.filletArc"),sQuery(id+"F24.wireOp",EDGE,"E95.filletArc"),sQuery(id+"F24.wireOp",EDGE,"E96.filletArc"),sQuery(id+"F24.wireOp",EDGE,"E97.filletArc"),sQuery(id+"F24.wireOp",EDGE,"E98.filletArc"),sQuery(id+"F24.wireOp",EDGE,"E99.filletArc"),sQuery(id+"F24.wireOp",EDGE,"E100.filletArc"),sQuery(id+"F24.wireOp",EDGE,"E101.filletArc"),sQuery(id+"F24.wireOp",EDGE,"E102.filletArc"),sQuery(id+"F24.wireOp",EDGE,"E103.filletArc"),sQuery(id+"F24.wireOp",EDGE,"E104.filletArc"),sQuery(id+"F24.wireOp",EDGE,"E105.filletArc"),sQuery(id+"F24.wireOp",EDGE,"E106.filletArc")])],"isStart":false});
            var sketch = newSketch(context, id + "F26", { "sketchPlane" : qUnion([Q0])});
            skCircle(sketch, "E107", {"center": v(33.42, 22.06) * mm, "radius": 2.6 * mm});
            skCircle(sketch, "E108", {"center": v(33.42, 22.06) * mm, "radius": 6.5 * mm});
            skSolve(sketch);
        }
        {
            var Q0;
            Q0=makeQuery(id+"F26.imprint","IMPRINT",FACE,{"disambiguationData":[TD([[makeQuery(id+"F26.imprint","IMPRINT",EDGE,{"derivedFrom":sQuery(id+"F26.wireOp",EDGE,"E107")}),-1.0]])]});
            extrude(context, id + "F27", {"entities" : qUnion([Q0]), "operationType" : NewBodyOperationType.ADD, "depth" : 1 * mm, "offsetDistance" : 25 * mm});
        }
    });
